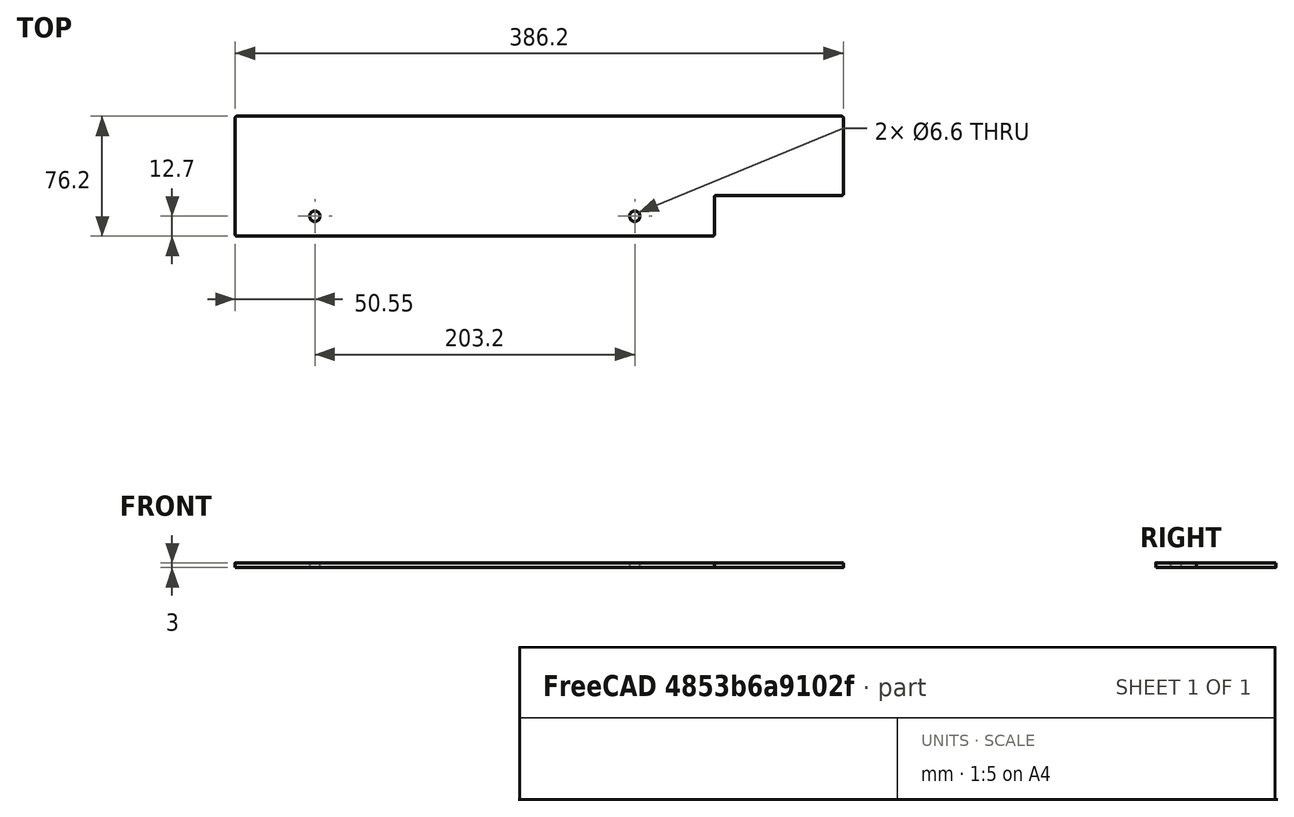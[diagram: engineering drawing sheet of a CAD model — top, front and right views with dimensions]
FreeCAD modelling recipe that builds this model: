
FCSTD DOCUMENT  (FreeCAD 0.20R29603 (Git))
Label: right_wall_front_24in
License: All rights reserved
LicenseURL: http://en.wikipedia.org/wiki/All_rights_reserved
objects: Spreadsheet::Sheet×1, Sketcher::SketchObject×1, PartDesign::Pad×1, PartDesign::Body×1
note: 4 computed .brp shape members not serialized (recipe doc carries the construction recipe); baked Part::Feature solids carry a one-line shape summary decoded from their .brp

FEATURE [Spreadsheet::Sheet] Spreadsheet
  cells = A2=Parameters; A3=DistanceFrontToDoor; B3(DistanceFrontToDoor)==386.7mm; A4=DistanceFrontToBracket; B4(DistanceFrontToBracket)==304.8mm; A5=LengthMargin; B5(LengthMargin)==0.5mm; A6=LengthFrontToDoor; B6(LengthFrontToDoor)==DistanceFrontToDoor - LengthMargin; A7=LengthFrontToBracket; B7(LengthFrontToBracket)==DistanceFrontToBracket - LengthMargin; A8=Height; B8(Height)==3in; A9=Thickness; B9(Thickness)==3mm; A10=CutoutMargin; B10(CutoutMargin)==0.5mm; A11=CutoutHeight; B11(CutoutHeight)==1in + CutoutMargin; A12=FilletRadius; B12(FilletRadius)==1mm; A13=MountHoleDiameter; B13(MountHoleDiameter)==0.26in; A14=MountHoleDistanceFromBottom; B14(MountHoleDistanceFromBottom)==0.5in; A15=MountHoleSpacing; B15(MountHoleSpacing)==4in
FEATURE [Sketcher::SketchObject] Sketch
  FullyConstrained = true
  MapMode = 5
  Support = -> [XY_Plane]
  expr: Constraints[14] = Spreadsheet.FilletRadius
  expr: Constraints[20] = Spreadsheet.Height
  expr: Constraints[44] = Spreadsheet.MountHoleDistanceFromBottom
  expr: Constraints[50] = Spreadsheet.MountHoleSpacing
  expr: Constraints[54] = Spreadsheet.MountHoleDiameter
  expr: Constraints[7] = Spreadsheet.LengthFrontToDoor
  expr: Constraints[8] = Spreadsheet.LengthFrontToBracket
  expr: Constraints[9] = Spreadsheet.CutoutHeight
  sketch-geometry (24):
    g0: LineSegment StartX=0 StartY=75.2 StartZ=0 EndX=0 EndY=1 EndZ=0
    g1: LineSegment StartX=1 StartY=0 StartZ=0 EndX=303.3 EndY=0 EndZ=0
    g2: LineSegment StartX=304.3 StartY=1 StartZ=0 EndX=304.3 EndY=24.9 EndZ=0
    g3: LineSegment StartX=305.3 StartY=25.9 StartZ=0 EndX=385.2 EndY=25.9 EndZ=0
    g4: LineSegment StartX=386.2 StartY=26.9 StartZ=0 EndX=386.2 EndY=75.2 EndZ=0
    g5: LineSegment StartX=385.2 StartY=76.2 StartZ=0 EndX=1 EndY=76.2 EndZ=0
    g6: ArcOfCircle CenterX=1 CenterY=75.2 CenterZ=0 NormalX=0 NormalY=0 NormalZ=1 AngleXU=0 Radius=1 StartAngle=1.5708 EndAngle=3.14159
    g7: GeomPoint X=0 Y=76.2 Z=0
    g8: ArcOfCircle CenterX=1 CenterY=1 CenterZ=0 NormalX=0 NormalY=0 NormalZ=1 AngleXU=0 Radius=1 StartAngle=3.14159 EndAngle=4.71239
    g9: GeomPoint X=0 Y=0 Z=0
    g10: ArcOfCircle CenterX=303.3 CenterY=1 CenterZ=0 NormalX=0 NormalY=0 NormalZ=1 AngleXU=0 Radius=1 StartAngle=4.71239 EndAngle=6.28319
    g11: GeomPoint X=304.3 Y=0 Z=0
    g12: ArcOfCircle CenterX=305.3 CenterY=24.9 CenterZ=0 NormalX=0 NormalY=0 NormalZ=1 AngleXU=0 Radius=1 StartAngle=1.5708 EndAngle=3.14159
    g13: GeomPoint X=304.3 Y=25.9 Z=0
    g14: ArcOfCircle CenterX=385.2 CenterY=26.9 CenterZ=0 NormalX=0 NormalY=0 NormalZ=1 AngleXU=0 Radius=1 StartAngle=4.71239 EndAngle=6.28319
    g15: GeomPoint X=386.2 Y=25.9 Z=0
    g16: ArcOfCircle CenterX=385.2 CenterY=75.2 CenterZ=0 NormalX=0 NormalY=0 NormalZ=1 AngleXU=0 Radius=1 StartAngle=-1.8e-15 EndAngle=1.5708
    g17: GeomPoint X=386.2 Y=76.2 Z=0
    g18: GeomPoint X=152.15 Y=0 Z=0
    g19: LineSegment StartX=152.15 StartY=0 StartZ=0 EndX=152.15 EndY=12.7 EndZ=0
    g20: LineSegment StartX=50.55 StartY=12.7 StartZ=0 EndX=152.15 EndY=12.7 EndZ=0
    g21: LineSegment StartX=152.15 StartY=12.7 StartZ=0 EndX=253.75 EndY=12.7 EndZ=0
    g22: Circle CenterX=50.55 CenterY=12.7 CenterZ=0 NormalX=0 NormalY=0 NormalZ=1 AngleXU=0 Radius=3.302
    g23: Circle CenterX=253.75 CenterY=12.7 CenterZ=0 NormalX=0 NormalY=0 NormalZ=1 AngleXU=0 Radius=3.302
  constraints (55):
    c: Vertical(g0)
    c: Horizontal(g1)
    c: Vertical(g2)
    c: Horizontal(g3)
    c: Vertical(g4)
    c: Horizontal(g5)
    c: Coincident(g-1,g9)
    c: DistanceX(g7,g17) = 386.2
    c: DistanceX(g9,g11) = 304.3
    c: DistanceY(g11,g13) = 25.9
    c: PointOnObject(g7,g0)
    c: PointOnObject(g7,g5)
    c: Tangent(g0,g6) = -1.5708
    c: Tangent(g5,g6) = -1.5708
    c: Radius(g6) = 1
    c: PointOnObject(g9,g0)
    c: PointOnObject(g9,g1)
    c: Tangent(g0,g8) = -1.5708
    c: Tangent(g1,g8) = -1.5708
    c: Equal(g8,g6)
    c: DistanceY(g1,g5) = 76.2
    c: PointOnObject(g11,g1)
    c: PointOnObject(g11,g2)
    c: Tangent(g1,g10) = -1.5708
    c: Tangent(g2,g10) = -1.5708
    c: Equal(g10,g8)
    c: PointOnObject(g13,g2)
    c: PointOnObject(g13,g3)
    c: Tangent(g2,g12) = 1.5708
    c: Tangent(g3,g12) = 1.5708
    c: Equal(g12,g10)
    c: PointOnObject(g15,g3)
    c: PointOnObject(g15,g4)
    c: Tangent(g3,g14) = -1.5708
    c: Tangent(g4,g14) = -1.5708
    c: Equal(g14,g12)
    c: PointOnObject(g17,g5)
    c: PointOnObject(g17,g4)
    c: Tangent(g5,g16) = -1.5708
    c: Tangent(g4,g16) = -1.5708
    c: Equal(g16,g14)
    c: Symmetric(g1,g1,g18)
    c: Coincident(g19,g18)
    c: Vertical(g19)
    c: DistanceY(g19,g19) = 12.7
    c: Horizontal(g20)
    c: Coincident(g20,g21)
    c: Horizontal(g21)
    c: Equal(g20,g21)
    c: Coincident(g19,g20)
    c: DistanceX(g20,g20) = 101.6
    c: Coincident(g22,g20)
    c: Coincident(g23,g21)
    c: Equal(g23,g22)
    c: Diameter(g23) = 6.604
FEATURE [PartDesign::Pad] Pad
  Direction = (0,0,1)
  Length = 3
  Length2 = 10
  Profile = -> Sketch
  ReferenceAxis = -> Sketch [N_Axis]
  Type = 0
  expr: Length = Spreadsheet.Thickness
FEATURE [PartDesign::Body] Body
  Group = -> [Sketch,Pad]
  Origin = -> Origin
  Tip = -> Pad
